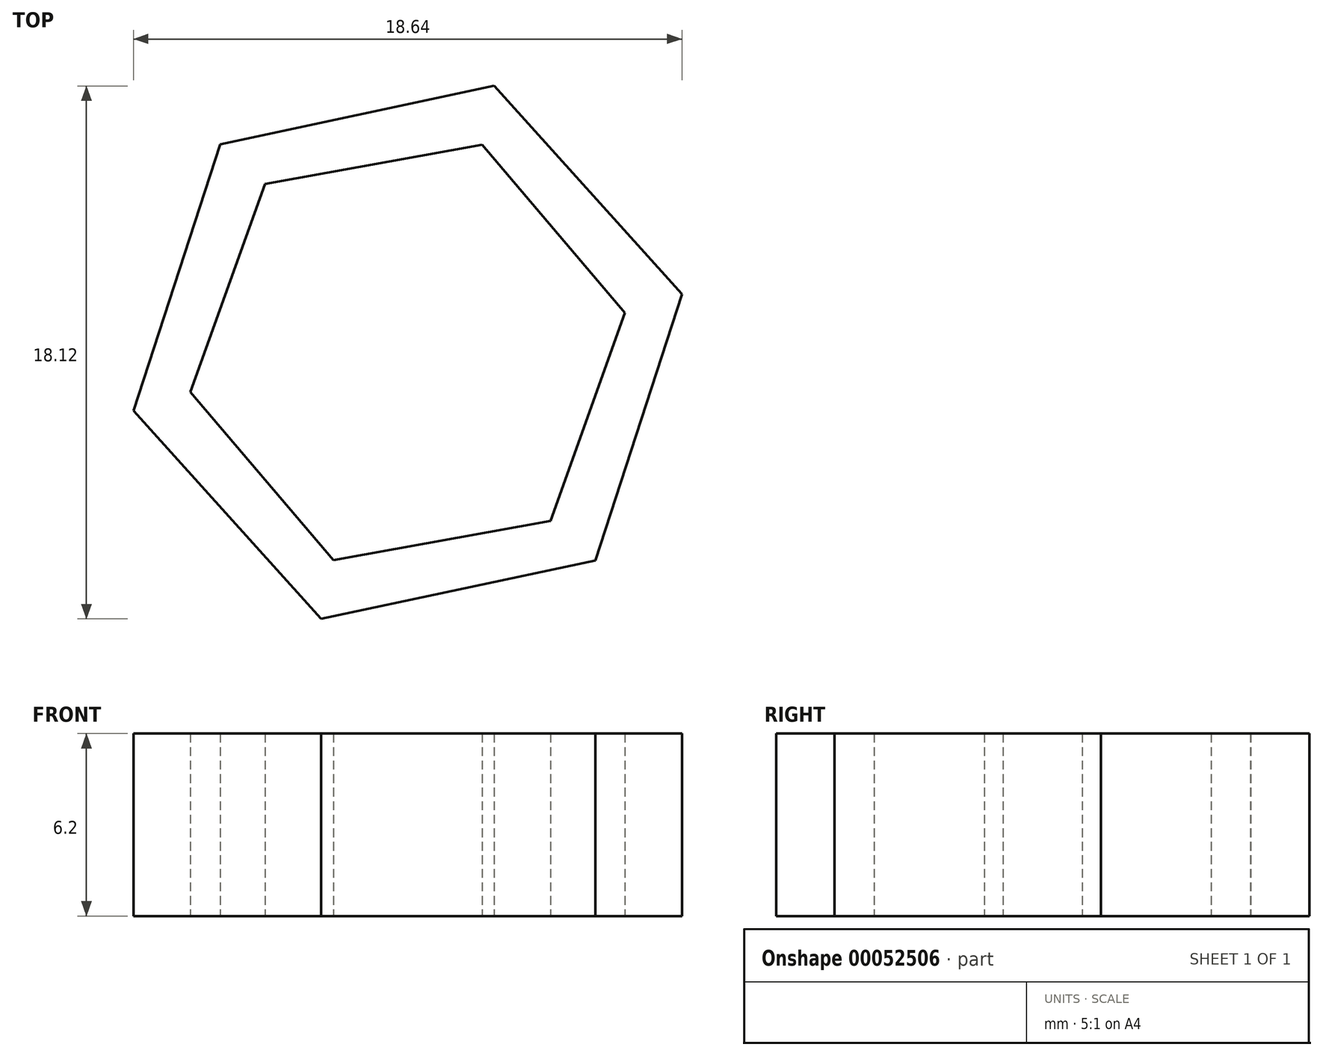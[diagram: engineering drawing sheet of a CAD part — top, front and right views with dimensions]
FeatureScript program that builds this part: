
annotation { "Feature Type Name" : "Feature", "Feature Type Description" : "" }
export const myFeature = defineFeature(function(context is Context, id is Id, definition is map)
    precondition{}
    {
        {
            var Q0;
            Q0=qCreatedBy(makeId("Top.planeOp"),FACE);
            var sketch = newSketch(context, id + "F0", { "sketchPlane" : qUnion([Q0])});
            skCircle(sketch, "E0.cCircle", {"center": v(0, 0) * mm, "radius": 7.5 * mm, "construction": true});
            skLineSegment(sketch, "E0.0", {"start": v(-4.86, 5.72) * mm, "end": v(2.53, 7.07) * mm});
            skLineSegment(sketch, "E0.1", {"start": v(2.53, 7.07) * mm, "end": v(7.38, 1.34) * mm});
            skLineSegment(sketch, "E0.2", {"start": v(7.38, 1.34) * mm, "end": v(4.86, -5.72) * mm});
            skLineSegment(sketch, "E0.3", {"start": v(4.86, -5.72) * mm, "end": v(-2.53, -7.07) * mm});
            skLineSegment(sketch, "E0.4", {"start": v(-2.53, -7.07) * mm, "end": v(-7.38, -1.34) * mm});
            skLineSegment(sketch, "E0.5", {"start": v(-7.38, -1.34) * mm, "end": v(-4.86, 5.72) * mm});
            skCircle(sketch, "E1.cCircle", {"center": v(0, 0) * mm, "radius": 9.53 * mm, "construction": true});
            skLineSegment(sketch, "E1.0", {"start": v(-6.38, 7.08) * mm, "end": v(2.94, 9.06) * mm});
            skLineSegment(sketch, "E1.1", {"start": v(2.94, 9.06) * mm, "end": v(9.32, 1.99) * mm});
            skLineSegment(sketch, "E1.2", {"start": v(9.32, 1.99) * mm, "end": v(6.38, -7.08) * mm});
            skLineSegment(sketch, "E1.3", {"start": v(6.38, -7.08) * mm, "end": v(-2.94, -9.06) * mm});
            skLineSegment(sketch, "E1.4", {"start": v(-2.94, -9.06) * mm, "end": v(-9.32, -1.99) * mm});
            skLineSegment(sketch, "E1.5", {"start": v(-9.32, -1.99) * mm, "end": v(-6.38, 7.08) * mm});
            skSolve(sketch);
        }
        {
            var Q0;
            Q0 = qSketchRegion(id + "F0", true);
            extrude(context, id + "F1", {"entities" : qUnion([Q0]), "depth" : 6.2 * mm});
        }
    });
